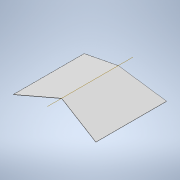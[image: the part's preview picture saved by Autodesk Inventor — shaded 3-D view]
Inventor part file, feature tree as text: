
AUTODESK INVENTOR PART (.ipt)
format: ipt  version: 2022.1 (Build 261234000, 234)  size: 112,128 bytes
history: native  units: in
note: dims shown in document units (in); Inventor stores cm internally (conversion verified against a paired STEP export)
features: plane x2, sketch x2, extrude x2
ambient origin geometry x8: Origin, YZ Plane, XZ Plane, XY Plane, X Axis, Y Axis, Z Axis, Center Point
bodies: Body1 (feature_tree)
feature tree (6):
  plane  "Work Plane3"
  sketch  "Sketch5"  dims[d11=0.1267in d14=216.0in]
  plane  "Work Plane4"
  sketch  "Sketch6"  dims[d15=166.0in d18=270.0in d19=-0.1267in d20=216.0in d21=270.0in d22=166.0in d23=1.0in d24=0.0in d25=1.0in d26=0.0in]
  extrude  "Extrusion3"  Depth=216.0in
  extrude  "Extrusion4"  Depth=1.0in
